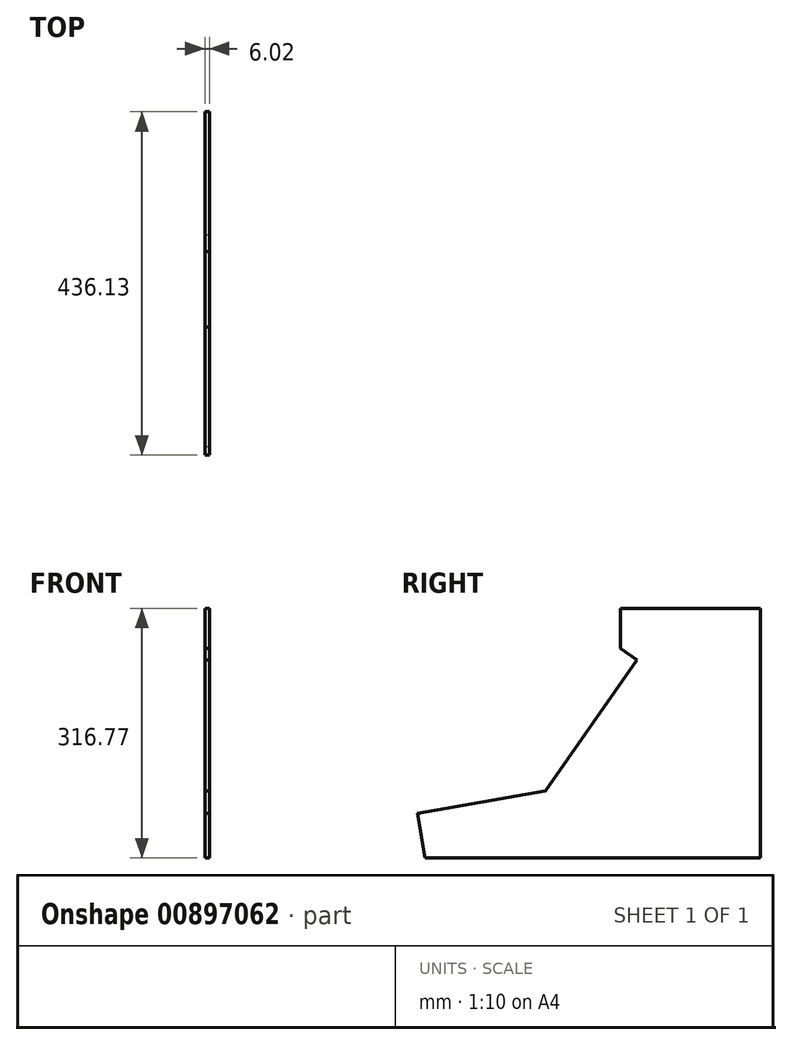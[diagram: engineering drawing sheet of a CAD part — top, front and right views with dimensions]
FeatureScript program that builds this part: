
annotation { "Feature Type Name" : "Feature", "Feature Type Description" : "" }
export const myFeature = defineFeature(function(context is Context, id is Id, definition is map)
    precondition{}
    {
        {
            var Q0;
            Q0=qCreatedBy(makeId("Right.planeOp"),FACE);
            var sketch = newSketch(context, id + "F0", { "sketchPlane" : qUnion([Q0])});
            skLineSegment(sketch, "E0", {"start": v(-9.92, 56.28) * mm, "end": v(152.67, 84.95) * mm});
            skLineSegment(sketch, "E1", {"start": v(152.67, 84.95) * mm, "end": v(269.22, 251.4) * mm});
            skLineSegment(sketch, "E2", {"start": v(248.41, 265.97) * mm, "end": v(248.41, 316.77) * mm});
            skLineSegment(sketch, "E3", {"start": v(248.41, 316.77) * mm, "end": v(426.21, 316.77) * mm});
            skLineSegment(sketch, "E4", {"start": v(426.21, 316.77) * mm, "end": v(426.21, 0) * mm});
            skLineSegment(sketch, "E5", {"start": v(426.21, 0) * mm, "end": v(0, 0) * mm});
            skLineSegment(sketch, "E6", {"start": v(-9.92, 56.28) * mm, "end": v(0, 0) * mm});
            skLineSegment(sketch, "E7", {"start": v(248.41, 265.97) * mm, "end": v(269.22, 251.4) * mm});
            skSolve(sketch);
        }
        {
            var Q0;
            Q0 = qSketchRegion(id + "F0", true);
            extrude(context, id + "F1", {"entities" : qUnion([Q0]), "depth" : 6.02 * mm, "offsetDistance" : 25.4 * mm});
        }
    });
